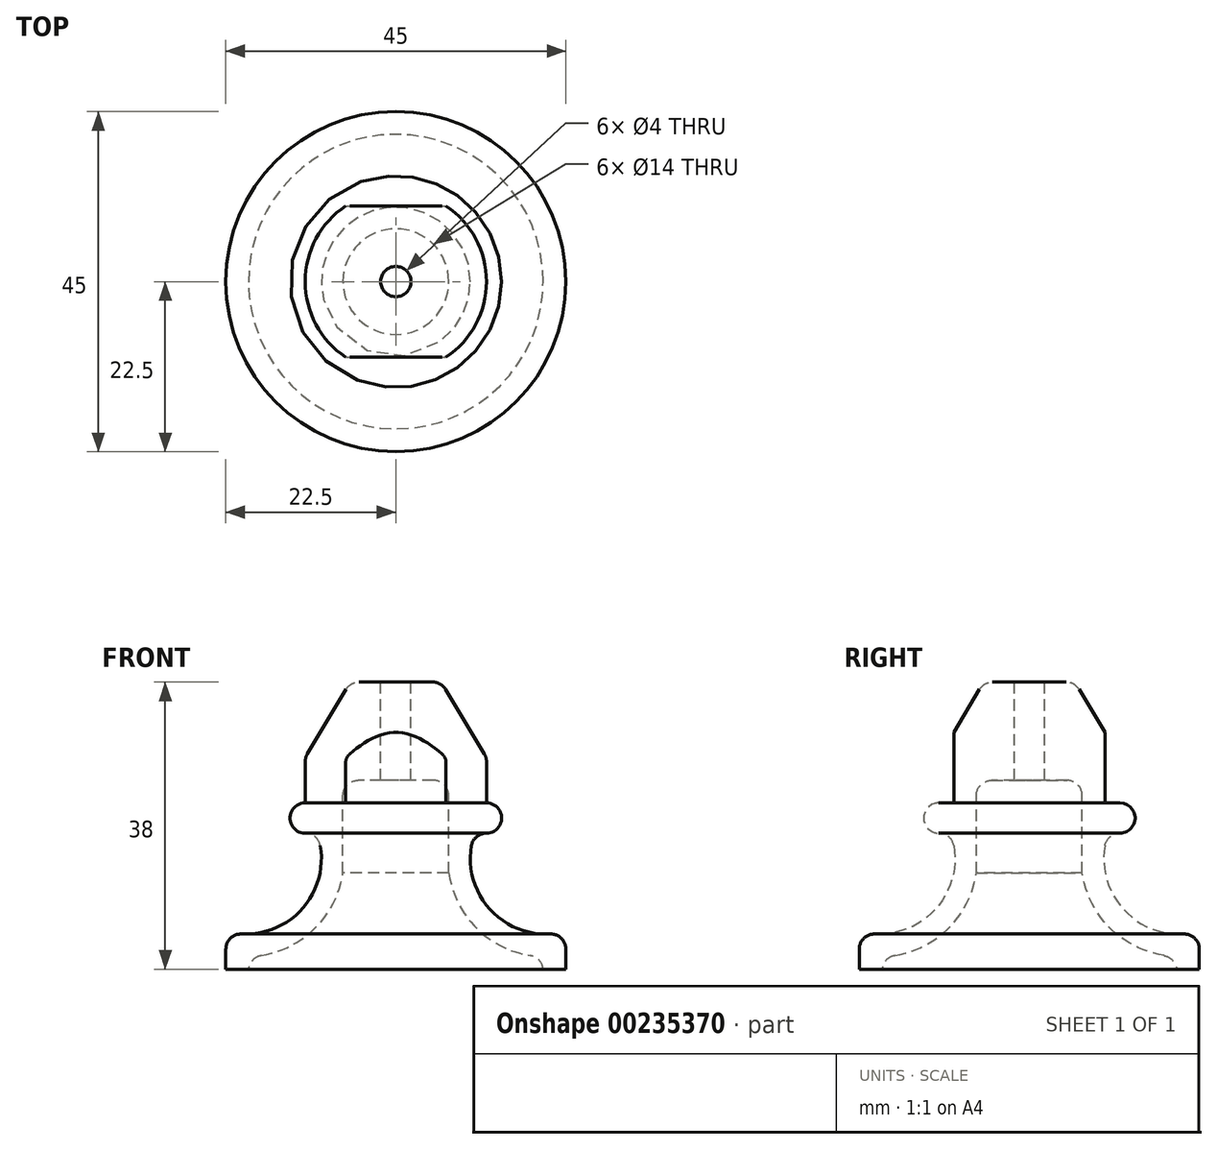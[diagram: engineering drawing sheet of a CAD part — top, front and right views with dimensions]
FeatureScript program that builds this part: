
annotation { "Feature Type Name" : "Feature", "Feature Type Description" : "" }
export const myFeature = defineFeature(function(context is Context, id is Id, definition is map)
    precondition{}
    {
        {
            var Q0;
            Q0=qCreatedBy(makeId("Front.planeOp"),FACE);
            var sketch = newSketch(context, id + "F0", { "sketchPlane" : qUnion([Q0])});
            skLineSegment(sketch, "E0", {"start": v(2, 38) * mm, "end": v(4.87, 38) * mm});
            skLineSegment(sketch, "E1", {"start": v(6.58, 37.03) * mm, "end": v(11.71, 28.48) * mm});
            skLineSegment(sketch, "E2", {"start": v(12, 27.45) * mm, "end": v(12, 22) * mm});
            skArc(sketch, "E3", {"start": v(12, 18) * mm, "mid": v(14, 20) * mm, "end": v(12, 22) * mm});
            skLineSegment(sketch, "E4", {"start": v(12, 18) * mm, "end": v(11.97, 18) * mm});
            skArc(sketch, "E5", {"start": v(10, 16.34) * mm, "mid": v(12.38, 8) * mm, "end": v(20.4, 4.66) * mm});
            skLineSegment(sketch, "E6", {"start": v(22.5, 2.66) * mm, "end": v(22.5, 0) * mm});
            skLineSegment(sketch, "E7", {"start": v(0, 38) * mm, "end": v(0, 0) * mm});
            skLineSegment(sketch, "E8", {"start": v(0, 0) * mm, "end": v(22.5, 0) * mm});
            skPoint(sketch, "E9.visualSharp", {"position": v(22.5, 5) * mm});
            skArc(sketch, "E9.filletArc", {"start": v(22.5, 2.66) * mm, "mid": v(21.88, 4.11) * mm, "end": v(20.4, 4.66) * mm});
            skPoint(sketch, "E10.visualSharp", {"position": v(10.44, 18) * mm});
            skArc(sketch, "E10.filletArc", {"start": v(11.97, 18) * mm, "mid": v(10.68, 17.53) * mm, "end": v(10, 16.34) * mm});
            skPoint(sketch, "E11", {"position": v(15, 20) * mm});
            skPoint(sketch, "E12.visualSharp", {"position": v(6, 38) * mm});
            skArc(sketch, "E12.filletArc", {"start": v(6.58, 37.03) * mm, "mid": v(5.85, 37.74) * mm, "end": v(4.87, 38) * mm});
            skLineSegment(sketch, "E13", {"start": v(2, 38) * mm, "end": v(2, 25) * mm});
            skLineSegment(sketch, "E14", {"start": v(2, 25) * mm, "end": v(0, 25) * mm});
            skLineSegment(sketch, "E15", {"start": v(0, 25) * mm, "end": v(5, 25) * mm});
            skLineSegment(sketch, "E16", {"start": v(7, 23) * mm, "end": v(7, 12.7) * mm});
            skPoint(sketch, "E17.visualSharp", {"position": v(7, 25) * mm});
            skArc(sketch, "E17.filletArc", {"start": v(7, 23) * mm, "mid": v(6.41, 24.41) * mm, "end": v(5, 25) * mm});
            skLineSegment(sketch, "E18.0", {"start": v(19.5, 0) * mm, "end": v(19.5, -0.17) * mm});
            skArc(sketch, "E18.1", {"start": v(7, 12.7) * mm, "mid": v(10.62, 5.49) * mm, "end": v(17.81, 1.8) * mm});
            skPoint(sketch, "E19.visualSharp", {"position": v(19.5, 1.65) * mm});
            skArc(sketch, "E19.filletArc", {"start": v(19.5, -0.17) * mm, "mid": v(19.02, 1.13) * mm, "end": v(17.81, 1.8) * mm});
            skPoint(sketch, "E20.visualSharp", {"position": v(12, 28) * mm});
            skArc(sketch, "E20.filletArc", {"start": v(12, 27.45) * mm, "mid": v(11.93, 27.98) * mm, "end": v(11.71, 28.48) * mm});
            skSolve(sketch);
        }
        {
            var Q0;
            Q0=makeQuery(id+"F0.imprint","IMPRINT",FACE,{"disambiguationData":[TD([[makeQuery(id+"F0.imprint","IMPRINT",EDGE,{"derivedFrom":sQuery(id+"F0.wireOp",EDGE,"E0")}),-1.0]])]});
            var Q1;
            Q1 = qSketchRegion(id + "F70UdmbQx8ZLp6X_1", true);
            var Q2;
            Q2=sQuery(id+"F0.wireOp",EDGE,"E7");
            revolve(context, id + "F1", {"entities" : qUnion([Q0, Q1]), "axis" : qUnion([Q2]), "revolveType" : RevolveType.FULL});
        }
        {
            var Q0;
            Q0=qCreatedBy(makeId("Right.planeOp"),FACE);
            var sketch = newSketch(context, id + "F2", { "sketchPlane" : qUnion([Q0])});
            skLineSegment(sketch, "E21", {"start": v(-11.71, 28.48) * mm, "end": v(-6.58, 37.03) * mm, "construction": true});
            skLineSegment(sketch, "E22", {"start": v(6.58, 37.03) * mm, "end": v(11.71, 28.48) * mm, "construction": true});
            skLineSegment(sketch, "E23", {"start": v(12, 27.45) * mm, "end": v(12, 22) * mm, "construction": true});
            skLineSegment(sketch, "E24", {"start": v(-12, 22) * mm, "end": v(-12, 27.45) * mm, "construction": true});
            skLineSegment(sketch, "E25", {"start": v(12, 22) * mm, "end": v(-12, 22) * mm, "construction": true});
            skLineSegment(sketch, "E26.bottom", {"start": v(-10, 22) * mm, "end": v(-22.22, 22) * mm});
            skLineSegment(sketch, "E26.top", {"start": v(-10, 38.86) * mm, "end": v(-22.22, 38.86) * mm});
            skLineSegment(sketch, "E26.left", {"start": v(-10, 22) * mm, "end": v(-10, 38.86) * mm});
            skLineSegment(sketch, "E26.right", {"start": v(-22.22, 22) * mm, "end": v(-22.22, 38.86) * mm});
            skLineSegment(sketch, "E27.bottom", {"start": v(10, 22) * mm, "end": v(19.15, 22) * mm});
            skLineSegment(sketch, "E27.top", {"start": v(10, 41.14) * mm, "end": v(19.15, 41.14) * mm});
            skLineSegment(sketch, "E27.left", {"start": v(10, 22) * mm, "end": v(10, 41.14) * mm});
            skLineSegment(sketch, "E27.right", {"start": v(19.15, 22) * mm, "end": v(19.15, 41.14) * mm});
            skSolve(sketch);
        }
        {
            var Q0;
            Q0=makeQuery(id+"F2.imprint","IMPRINT",FACE,{"disambiguationData":[TD([[makeQuery(id+"F2.imprint","IMPRINT",EDGE,{"derivedFrom":sQuery(id+"F2.wireOp",EDGE,"E27.bottom")}),1.0]])]});
            var Q1;
            Q1=makeQuery(id+"F2.imprint","IMPRINT",FACE,{"disambiguationData":[TD([[makeQuery(id+"F2.imprint","IMPRINT",EDGE,{"derivedFrom":sQuery(id+"F2.wireOp",EDGE,"E26.bottom")}),-1.0]])]});
            extrude(context, id + "F3", {"entities" : qUnion([Q0, Q1]), "operationType" : NewBodyOperationType.REMOVE, "oppositeDirection" : true, "depth" : 25 * mm, "hasSecondDirection" : true, "secondDirectionOppositeDirection" : false, "secondDirectionDepth" : 25 * mm});
        }
    });
